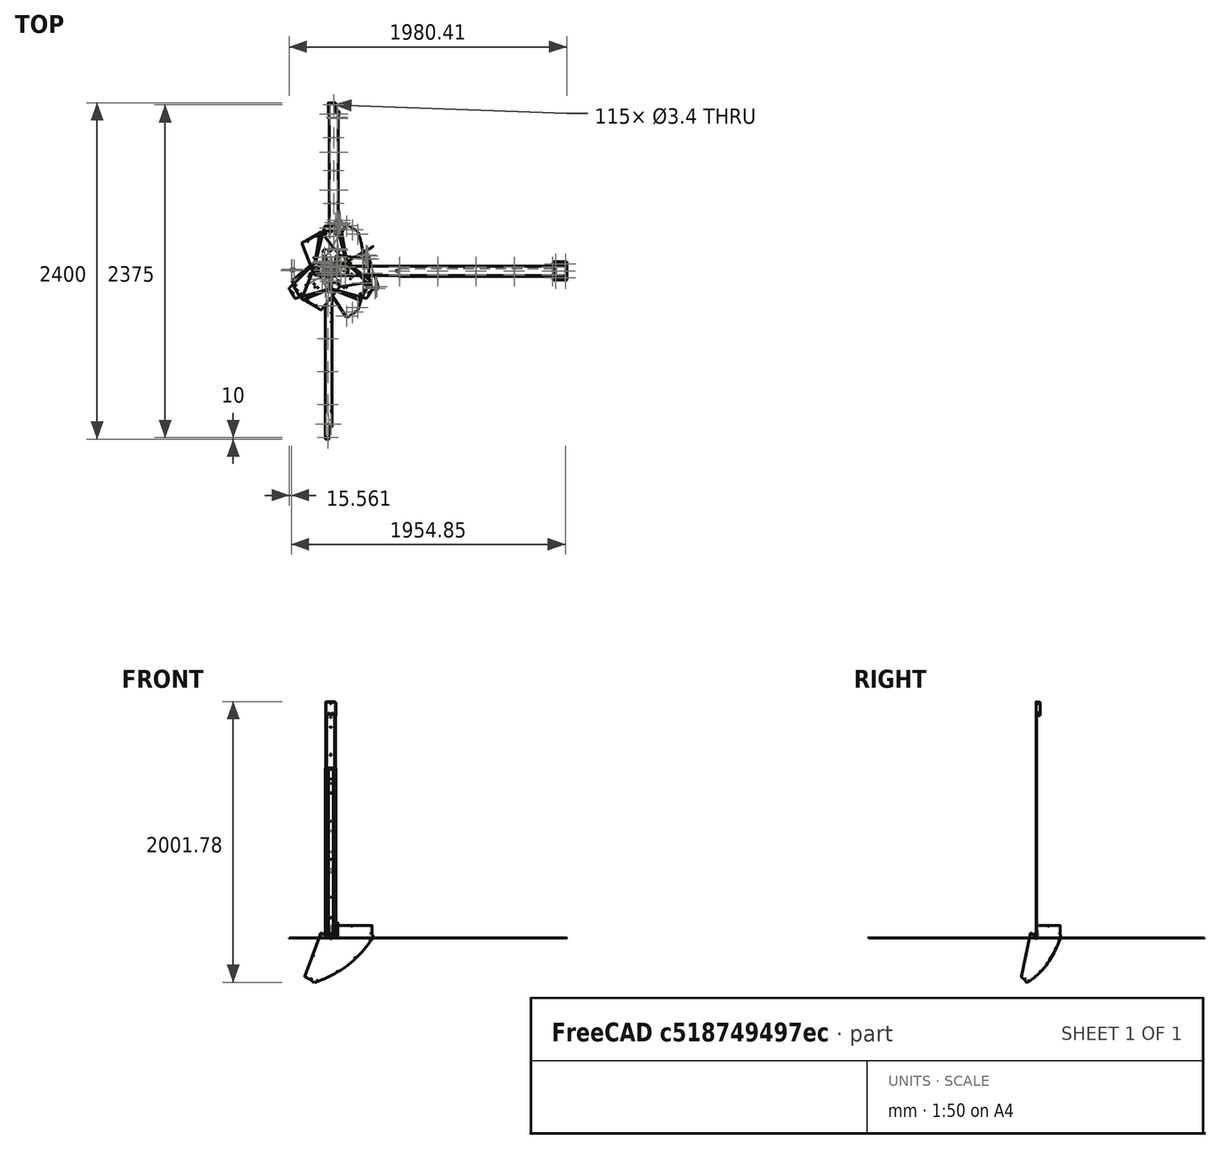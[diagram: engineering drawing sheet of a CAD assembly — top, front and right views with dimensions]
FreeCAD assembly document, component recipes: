
FREECAD ASSEMBLY — COMPONENT RECIPES ("composit_full_size3_ss_unfold")

This assembly document has 28 components, labeled P0..P27 below (a component is one placed body or linked part). 3 of them carry a construction recipe — the FreeCAD feature program that regenerates the part from scratch, quoted from this document or its linked companion documents; the rest are supplied as boundary geometry only. No exploded tour is included for this assembly.
COMPONENT P0 — recipe-attached ("Body", modeled in this document).
Construction recipe (the document's own serialized feature program — sketch geometry with constraints, then the solid features built on it; lengths are millimeters unless a unit is written):

FEATURE [PartDesign::FeatureBase] BaseFeature
  BaseFeature = -> Unfold
  Placement = pos=(0,0,0) rot=(-0.056475,0.056475,-0.996805;1.574rad)
  Suppressed = false
  expr: Placement = .BaseFeature.Placement
FEATURE [PartDesign::SubShapeBinder] Binder
  BindCopyOnChange = 0
  BindMode = 0
  ClaimChildren = false
  Context = -> Body [Binder.]
  Fuse = false
  MakeFace = true
  OffsetFill = false
  OffsetIntersection = false
  OffsetJoinType = 0
  OffsetOpenResult = false
  PartialLoad = false
  Relative = true
  Support = -> [Unfold_Sketch_bends]
  _Version = 2
FEATURE [Sketcher::SketchObject] Sketch
  AttachmentSupport = -> [XY_Plane]
  ExternalGeometry = -> [Binder]
  FullyConstrained = false
  MapMode = 5
  sketch-geometry (9):
    g0: Circle CenterX=172.913 CenterY=-294.074 CenterZ=0 NormalX=0 NormalY=0 NormalZ=1 AngleXU=0 Radius=1
    g1: Circle CenterX=4.76114 CenterY=-4.69033 CenterZ=0 NormalX=0 NormalY=0 NormalZ=1 AngleXU=0 Radius=1
    g2: Circle CenterX=4.76114 CenterY=4.69033 CenterZ=0 NormalX=0 NormalY=0 NormalZ=1 AngleXU=0 Radius=1
    g3: Circle CenterX=172.913 CenterY=294.074 CenterZ=0 NormalX=0 NormalY=0 NormalZ=1 AngleXU=0 Radius=1
    g4: LineSegment StartX=172.225 StartY=-294.474 StartZ=0 EndX=172.913 EndY=-294.074 EndZ=0
    g5: LineSegment StartX=4.07262 StartY=-5.0904 StartZ=0 EndX=4.76114 EndY=-4.69033 EndZ=0
    g6: LineSegment StartX=4.07262 StartY=5.0904 StartZ=0 EndX=4.76114 EndY=4.69033 EndZ=0
    g7: ArcOfCircle CenterX=1.01937 CenterY=5.2064e-12 CenterZ=0 NormalX=0 NormalY=0 NormalZ=1 AngleXU=0 Radius=6 StartAngle=5.25252 EndAngle=7.31385
    g8: LineSegment StartX=172.225 StartY=294.474 StartZ=0 EndX=172.913 EndY=294.074 EndZ=0
  constraints (25):
    c: Diameter(g0) = 2
    c: Equal(g0,g1)
    c: Equal(g1,g2)
    c: Equal(g2,g3)
    c: Coincident(g4,g-3)
    c: Coincident(g4,g0)
    c: Perpendicular(g-3,g4)
    c: Distance(g4) = 0.796314
    c: PointOnObject(g5,g-3)
    c: Perpendicular(g-3,g5)
    c: PointOnObject(g6,g-4)
    c: Perpendicular(g-4,g6)
    c: Coincident(g7,g-3)
    c: Coincident(g7,g-4)
    c: Coincident(g2,g6)
    c: PointOnObject(g2,g7)
    c: Radius(g7) = 6
    c: Coincident(g5,g1)
    c: PointOnObject(g1,g7)
    c: Equal(g5,g6)
    c: Equal(g6,g4)
    c: Coincident(g8,g-4)
    c: Coincident(g8,g3)
    c: Perpendicular(g-4,g8)
    c: Equal(g8,g6)
FEATURE [PartDesign::Pocket] Pocket
  BaseFeature = -> BaseFeature
  Direction = (0,0,-1)
  Length = 5
  Length2 = 5
  Midplane = true
  Placement = pos=(0,0,0) rot=(-0.056475,0.056475,-0.996805;1.574rad)
  Profile = -> Sketch
  ReferenceAxis = -> Sketch [N_Axis]
  Suppressed = false
  Type = 1
FEATURE [PartDesign::Body] Body
  BaseFeature = -> Unfold
  Group = -> [BaseFeature,Binder,Sketch,Pocket]
  Origin = -> Origin
  Tip = -> Pocket
COMPONENT P1 — recipe-attached ("pillar_top_Body", modeled in this document).
Construction recipe (the document's own serialized feature program — sketch geometry with constraints, then the solid features built on it; lengths are millimeters unless a unit is written):

FEATURE [PartDesign::SubShapeBinder] Binder001
  BindCopyOnChange = 0
  BindMode = 0
  ClaimChildren = false
  Context = -> Body001 [Binder001.]
  Fuse = false
  MakeFace = true
  OffsetFill = false
  OffsetIntersection = false
  OffsetJoinType = 0
  OffsetOpenResult = false
  PartialLoad = false
  Relative = true
  Support = -> [Unfold_Sketch_bends023]
  _Version = 2
  expr: Support = <<pillar_top_Sketch_bends>>._self
FEATURE [Sketcher::SketchObject] Sketch001
  AttachmentSupport = -> [XY_Plane001]
  ExternalGeometry = -> [Binder001]
  FullyConstrained = true
  MapMode = 5
  sketch-geometry (6):
    g0: Circle CenterX=-34.042 CenterY=-80.0841 CenterZ=0 NormalX=0 NormalY=0 NormalZ=1 AngleXU=0 Radius=1
    g1: Circle CenterX=34.042 CenterY=-80.0841 CenterZ=0 NormalX=0 NormalY=0 NormalZ=1 AngleXU=0 Radius=1
    g2: Circle CenterX=34.042 CenterY=-0.0840704 CenterZ=0 NormalX=0 NormalY=0 NormalZ=1 AngleXU=0 Radius=1
    g3: Circle CenterX=32 CenterY=1.95796 CenterZ=0 NormalX=0 NormalY=0 NormalZ=1 AngleXU=0 Radius=1
    g4: Circle CenterX=-32 CenterY=1.95796 CenterZ=0 NormalX=0 NormalY=0 NormalZ=1 AngleXU=0 Radius=1
    g5: Circle CenterX=-34.042 CenterY=-0.0840704 CenterZ=0 NormalX=0 NormalY=0 NormalZ=1 AngleXU=0 Radius=1
  constraints (12):
    c: Coincident(g0,g-5)
    c: Coincident(g1,g-6)
    c: Coincident(g2,g-6)
    c: Coincident(g3,g-3)
    c: Coincident(g4,g-4)
    c: Coincident(g5,g-5)
    c: Equal(g0,g1)
    c: Equal(g0,g2)
    c: Equal(g0,g3)
    c: Equal(g0,g5)
    c: Equal(g0,g4)
    c: Diameter(g0) = 2
FEATURE [PartDesign::FeatureBase] BaseFeature001
  BaseFeature = -> Unfold023
  Suppressed = false
  expr: BaseFeature = <<pillar_top_Unfold>>._self
FEATURE [PartDesign::Pocket] Pocket001
  BaseFeature = -> BaseFeature001
  Direction = (0,0,-1)
  Length = 5
  Length2 = 5
  Profile = -> Sketch001
  ReferenceAxis = -> Sketch001 [N_Axis]
  Reversed = true
  Suppressed = false
  Type = 0
FEATURE [PartDesign::Body] Body001  label="pillar_top_Body"
  Group = -> [BaseFeature001,Binder001,Sketch001,Pocket001]
  Origin = -> Origin001
  Tip = -> Pocket001
COMPONENT P2 — geometry summary ("Body002"; no construction recipe available for this part):
  bounding box: 102.9 x 96.0 x 0.5 mm
  tessellated surface: 412 triangles
  volume: 4717 mm^3 (96% of its bounding box)
  symmetry: mirror-symmetric across its z mid-plane
COMPONENT P3 — geometry summary ("pillar_Body"; no construction recipe available for this part):
  bounding box: 1684.0 x 75.0 x 2.0 mm
  tessellated surface: 1,560 triangles
  volume: 225558 mm^3 (89% of its bounding box)
  symmetry: 2-fold rotationally symmetric about the x axis; 2-fold rotationally symmetric about the y axis; 2-fold rotationally symmetric about the z axis; mirror-symmetric across its x mid-plane, y mid-plane, z mid-plane
COMPONENT P4 — geometry summary ("pillar_bottom_Body"; no construction recipe available for this part):
  bounding box: 131.1 x 101.0 x 2.0 mm
  tessellated surface: 800 triangles
  volume: 11774 mm^3 (44% of its bounding box)
  symmetry: mirror-symmetric across its z mid-plane
COMPONENT P5 — geometry summary ("dec_corner_Body"; no construction recipe available for this part):
  bounding box: 1113.0 x 56.5 x 0.5 mm
  tessellated surface: 572 triangles
  volume: 31373 mm^3 (100% of its bounding box)
  symmetry: 2-fold rotationally symmetric about the x axis; 2-fold rotationally symmetric about the y axis; 2-fold rotationally symmetric about the z axis; mirror-symmetric across its x mid-plane, y mid-plane, z mid-plane
COMPONENT P6 — geometry summary ("basement_amplifier_old_body"; no construction recipe available for this part):
  bounding box: 245.0 x 58.2 x 2.0 mm
  tessellated surface: 736 triangles
  volume: 27799 mm^3 (98% of its bounding box)
  symmetry: 2-fold rotationally symmetric about the x axis; 2-fold rotationally symmetric about the y axis; mirror-symmetric across its y mid-plane, z mid-plane
COMPONENT P7 — geometry summary ("door_conn_body"; no construction recipe available for this part):
  bounding box: 1200.0 x 78.8 x 1.0 mm
  tessellated surface: 1,212 triangles
  volume: 75758 mm^3 (80% of its bounding box)
  symmetry: mirror-symmetric across its z mid-plane
COMPONENT P8 — geometry summary ("door_base_pillar_to_hor_fix_body"; no construction recipe available for this part):
  bounding box: 44.9 x 40.5 x 1.0 mm
  tessellated surface: 472 triangles
  volume: 1128 mm^3 (62% of its bounding box)
  symmetry: mirror-symmetric across its z mid-plane
COMPONENT P9 — geometry summary ("door_hor_body"; no construction recipe available for this part):
  bounding box: 256.0 x 97.5 x 1.0 mm
  tessellated surface: 528 triangles
  volume: 9271 mm^3 (37% of its bounding box)
  symmetry: mirror-symmetric across its z mid-plane
COMPONENT P10 — geometry summary ("sink_material_0.30ansi"; no construction recipe available for this part):
  bounding box: 589.7 x 237.9 x 89.4 mm
  tessellated surface: 1,040 triangles
  volume: 66854 mm^3 (1% of its bounding box)
  symmetry: mirror-symmetric across its x mid-plane
COMPONENT P11 — geometry summary ("top_dec_corner_0.30ansi"; no construction recipe available for this part):
  bounding box: 96.0 x 75.5 x 29.0 mm
  tessellated surface: 448 triangles
  volume: 4725 mm^3 (2% of its bounding box)
COMPONENT P12 — geometry summary ("pillar_bottom_material_0.30ansi"; no construction recipe available for this part):
  bounding box: 101.0 x 80.0 x 25.0 mm
  tessellated surface: 792 triangles
  volume: 11019 mm^3 (5% of its bounding box)
COMPONENT P13 — geometry summary ("pillar_material_0.30ansi"; no construction recipe available for this part):
  bounding box: 1684.0 x 75.0 x 19.0 mm
  tessellated surface: 1,560 triangles
  volume: 229601 mm^3 (10% of its bounding box)
  symmetry: mirror-symmetric across its x mid-plane
COMPONENT P14 — recipe-attached ("dec_corner_0.30ansi", modeled in this document).
Construction recipe (the document's own serialized feature program — sketch geometry with constraints, then the solid features built on it; lengths are millimeters unless a unit is written):

FEATURE [Part::Feature] Unfold017
  Placement = pos=(0,0,0) rot=(0,0,1;0.523599rad)
  shape: bbox 481.5 x 552.9 x 2 mm, 69 faces (baked)
FEATURE [PartDesign::FeatureAdditivePython] PDW_Add001  # link proxy (typed FeaturePython)
  Body = Body013
  ClaimChildren = true
  EditPlacementAdjustments = false
  Enabled = 1
  LinkedObject = -> Unfold017
  MeshTolerance = 0.1
  PatternBaseOffset = 0
  PatternBaseScale = 1
  PatternBaseScaleXYZ = (1,1,1)
  PatternOffsetCut = false
  PatternOffsetIntersection = false
  PatternOffsetJoin = 0
  PatternOffsetMode = 0
  PatternOffsetSelfIntersection = false
  PatternOperation = 0
  PatternOperationDefault = None
  PatternScaleCut = false
  PatternShapeOffset = 0
  PatternShapeScale = 1
  PatternShapeScaleXYZ = (1,1,1)
  PatternToolOffset = 0
  PatternToolScale = 1
  PatternToolScaleXYZ = (1,1,1)
  RefineMesh = true
  ShapeManagement = 0
  ShowMeshProps = false
  ShowOffsetProps = false
  ShowScaleProps = false
  ShowWarnings = true
  Suppressed = false
  TipBaseOffset = 0
  TipBaseScale = 1
  TipBaseScaleXYZ = (1,1,1)
  TipOffsetCut = false
  TipOffsetIntersection = false
  TipOffsetJoin = 0
  TipOffsetMode = 0
  TipOffsetSelfIntersection = false
  TipOperation = 0
  TipOperationDefault = Fuse
  TipScaleCut = false
  TipShapeOffset = 0
  TipShapeScale = 1
  TipShapeScaleXYZ = (1,1,1)
  TipTool = -> Unfold017
  TipToolOffset = 0
  TipToolScale = 1
  TipToolScaleXYZ = (1,1,1)
  Type = Additive
  UsePatternBaseAddSubShape = false
  UsePatternToolAddSubShape = false
  UseTipBaseAddSubShape = false
  UseTipToolAddSubShape = false
  Version = 0.2023.08.13
FEATURE [Sketcher::SketchObject] Unfold_Sketch_bends017  label="basement2_amplifier_bends"
  FullyConstrained = false
  sketch-geometry (6):
    g0: LineSegment StartX=48.4571 StartY=82.0288 StartZ=0 EndX=273.448 EndY=46.699 EndZ=0
    g1: LineSegment StartX=273.448 StartY=-46.699 StartZ=0 EndX=48.4571 EndY=-82.0288 EndZ=0
    g2: LineSegment StartX=-96.2817 StartY=260.163 StartZ=0 EndX=46.8104 EndY=82.9795 EndZ=0
    g3: LineSegment StartX=46.8104 StartY=-82.9795 StartZ=0 EndX=-96.2817 EndY=-260.163 EndZ=0
    g4: LineSegment StartX=-95.2675 StartY=0.950723 StartZ=0 EndX=-177.167 EndY=213.464 EndZ=0
    g5: LineSegment StartX=-177.167 StartY=-213.464 StartZ=0 EndX=-95.2675 EndY=-0.950723 EndZ=0
FEATURE [Sketcher::SketchObject] Unfold_Sketch017  label="basement2_amplifier_Sketch"
  ExternalGeometry = -> [Unfold_Sketch_bends017]
  FullyConstrained = false
  sketch-geometry (79):
    g0: ArcOfCircle CenterX=70.1267 CenterY=101.256 CenterZ=0 NormalX=0 NormalY=0 NormalZ=1 AngleXU=2.98584 Radius=10 StartAngle=4.71239 EndAngle=5.91534
    g1: LineSegment StartX=268.589 StartY=80.2148 StartZ=0 EndX=71.678 EndY=111.135 EndZ=0
    g2: ArcOfCircle CenterX=267.037 CenterY=70.3358 CenterZ=0 NormalX=0 NormalY=0 NormalZ=1 AngleXU=2.98584 Radius=10 StartAngle=3.14159 EndAngle=4.71239
    g3: LineSegment StartX=61.4665 StartY=106.256 StartZ=0 EndX=48.8226 EndY=84.3564 EndZ=0
    g4: LineSegment StartX=48.0916 StartY=79.7011 StartZ=0 EndX=48.8226 EndY=84.3564 EndZ=0
    g5: LineSegment StartX=48.0916 StartY=79.7011 StartZ=0 EndX=46.188 EndY=80 EndZ=0
    g6: LineSegment StartX=46.188 StartY=80 StartZ=0 EndX=44.9774 EndY=81.4991 EndZ=0
    g7: LineSegment StartX=48.6435 StartY=84.4599 StartZ=0 EndX=61.2873 EndY=106.36 EndZ=0
    g8: ArcOfCircle CenterX=52.6271 CenterY=111.36 CenterZ=0 NormalX=0 NormalY=0 NormalZ=1 AngleXU=-0.891442 Radius=10 StartAngle=0.367843 EndAngle=1.5708
    g9: ArcOfCircle CenterX=-72.6061 CenterY=266.429 CenterZ=0 NormalX=0 NormalY=0 NormalZ=1 AngleXU=-0.891442 Radius=10 StartAngle=1.5708 EndAngle=3.14159
    g10: LineSegment StartX=60.4069 StartY=117.643 StartZ=0 EndX=-64.8263 EndY=272.712 EndZ=0
    g11: LineSegment StartX=48.6435 StartY=84.4599 StartZ=0 EndX=44.9774 EndY=81.4991 EndZ=0
    g12: LineSegment StartX=-98.1147 StartY=258.682 StartZ=0 EndX=-78.889 EndY=274.209 EndZ=0
    g13: LineSegment StartX=-98.1147 StartY=258.682 StartZ=0 EndX=-174.968 EndY=214.311 EndZ=0
    g14: LineSegment StartX=-198.027 StartY=205.424 StartZ=0 EndX=-174.968 EndY=214.311 EndZ=0
    g15: ArcOfCircle CenterX=-194.431 CenterY=196.093 CenterZ=0 NormalX=0 NormalY=0 NormalZ=1 AngleXU=-1.20295 Radius=10 StartAngle=3.14159 EndAngle=4.71239
    g16: LineSegment StartX=-203.762 StartY=192.497 StartZ=0 EndX=-132.085 EndY=6.50739 EndZ=0
    g17: ArcOfCircle CenterX=-122.754 CenterY=10.1034 CenterZ=0 NormalX=0 NormalY=0 NormalZ=1 AngleXU=-1.20295 Radius=10 StartAngle=4.71239 EndAngle=5.91534
    g18: LineSegment StartX=-122.754 StartY=0.103426 StartZ=0 EndX=-97.4661 EndY=0.103426 EndZ=0
    g19: LineSegment StartX=-93.069 StartY=1.79802 StartZ=0 EndX=-97.4661 EndY=0.103426 EndZ=0
    g20: LineSegment StartX=-93.069 StartY=1.79802 StartZ=0 EndX=-92.376 EndY=-7.26482e-10 EndZ=0
    g21: LineSegment StartX=-92.376 StartY=-7.26482e-10 StartZ=0 EndX=-93.069 EndY=-1.79802 EndZ=0
    g22: LineSegment StartX=-97.4661 StartY=-0.103426 StartZ=0 EndX=-93.069 EndY=-1.79802 EndZ=0
    g23: LineSegment StartX=-97.4661 StartY=-0.103426 StartZ=0 EndX=-122.754 EndY=-0.103426 EndZ=0
    g24: ArcOfCircle CenterX=-122.754 CenterY=-10.1034 CenterZ=0 NormalX=0 NormalY=0 NormalZ=1 AngleXU=1.20295 Radius=10 StartAngle=0.367843 EndAngle=1.5708
    g25: LineSegment StartX=-132.085 StartY=-6.50739 StartZ=0 EndX=-203.762 EndY=-192.497 EndZ=0
    g26: ArcOfCircle CenterX=-194.431 CenterY=-196.093 CenterZ=0 NormalX=0 NormalY=0 NormalZ=1 AngleXU=1.20295 Radius=10 StartAngle=1.5708 EndAngle=3.14159
    g27: LineSegment StartX=-174.968 StartY=-214.311 StartZ=0 EndX=-198.027 EndY=-205.424 EndZ=0
    g28: LineSegment StartX=-174.968 StartY=-214.311 StartZ=0 EndX=-98.1147 EndY=-258.682 EndZ=0
    g29: LineSegment StartX=-78.889 StartY=-274.209 StartZ=0 EndX=-98.1147 EndY=-258.682 EndZ=0
    g30: ArcOfCircle CenterX=-72.6061 CenterY=-266.429 CenterZ=0 NormalX=0 NormalY=0 NormalZ=1 AngleXU=0.891442 Radius=10 StartAngle=3.14159 EndAngle=4.71239
    g31: LineSegment StartX=-64.8263 StartY=-272.712 StartZ=0 EndX=60.4069 EndY=-117.643 EndZ=0
    g32: ArcOfCircle CenterX=52.6271 CenterY=-111.36 CenterZ=0 NormalX=0 NormalY=0 NormalZ=1 AngleXU=0.891442 Radius=10 StartAngle=4.71239 EndAngle=5.91534
    g33: LineSegment StartX=61.2873 StartY=-106.36 StartZ=0 EndX=48.6435 EndY=-84.4599 EndZ=0
    g34: LineSegment StartX=44.9774 StartY=-81.4991 StartZ=0 EndX=48.6435 EndY=-84.4599 EndZ=0
    g35: LineSegment StartX=44.9774 StartY=-81.4991 StartZ=0 EndX=46.188 EndY=-80 EndZ=0
    g36: LineSegment StartX=46.188 StartY=-80 StartZ=0 EndX=48.0916 EndY=-79.7011 EndZ=0
    g37: LineSegment StartX=48.8226 StartY=-84.3564 StartZ=0 EndX=48.0916 EndY=-79.7011 EndZ=0
    g38: LineSegment StartX=48.8226 StartY=-84.3564 StartZ=0 EndX=61.4665 EndY=-106.256 EndZ=0
    g39: ArcOfCircle CenterX=70.1267 CenterY=-101.256 CenterZ=0 NormalX=0 NormalY=0 NormalZ=1 AngleXU=-2.98584 Radius=10 StartAngle=0.367843 EndAngle=1.5708
    g40: LineSegment StartX=71.678 StartY=-111.135 StartZ=0 EndX=268.589 EndY=-80.2148 EndZ=0
    g41: ArcOfCircle CenterX=267.037 CenterY=-70.3358 CenterZ=0 NormalX=0 NormalY=0 NormalZ=1 AngleXU=-2.98584 Radius=10 StartAngle=1.5708 EndAngle=3.14159
    g42: LineSegment StartX=273.083 StartY=-44.3713 StartZ=0 EndX=276.916 EndY=-68.7846 EndZ=0
    g43: LineSegment StartX=273.083 StartY=44.3713 StartZ=0 EndX=273.083 EndY=-44.3713 EndZ=0
    g44: LineSegment StartX=276.916 StartY=68.7846 StartZ=0 EndX=273.083 EndY=44.3713 EndZ=0
    g45: Circle CenterX=34.575 CenterY=34.575 CenterZ=0 NormalX=0 NormalY=0 NormalZ=1 AngleXU=-1.5708 Radius=5.4
    g46: Circle CenterX=-34.575 CenterY=-34.575 CenterZ=0 NormalX=0 NormalY=0 NormalZ=1 AngleXU=-1.5708 Radius=5.4
    g47: Circle CenterX=34.575 CenterY=-34.575 CenterZ=0 NormalX=0 NormalY=0 NormalZ=1 AngleXU=-1.5708 Radius=5.4
    g48: Circle CenterX=-34.575 CenterY=34.575 CenterZ=0 NormalX=0 NormalY=0 NormalZ=1 AngleXU=-1.5708 Radius=5.4
    g49: Circle CenterX=265 CenterY=-36 CenterZ=0 NormalX=0 NormalY=0 NormalZ=1 AngleXU=-1.5708 Radius=2.5
    g50: Circle CenterX=265 CenterY=36 CenterZ=0 NormalX=0 NormalY=0 NormalZ=1 AngleXU=1.5708 Radius=2.5
    g51: Circle CenterX=55.7258 CenterY=68.9742 CenterZ=0 NormalX=0 NormalY=0 NormalZ=1 AngleXU=1.5708 Radius=2.5
    g52: Circle CenterX=140.207 CenterY=56.173 CenterZ=0 NormalX=0 NormalY=0 NormalZ=1 AngleXU=1.5708 Radius=2.5
    g53: Circle CenterX=-21.4561 CenterY=149.509 CenterZ=0 NormalX=0 NormalY=0 NormalZ=1 AngleXU=0.523599 Radius=2.5
    g54: Circle CenterX=-101.323 CenterY=247.497 CenterZ=0 NormalX=0 NormalY=0 NormalZ=1 AngleXU=0.523599 Radius=2.5
    g55: Circle CenterX=-87.5963 CenterY=13.7728 CenterZ=0 NormalX=0 NormalY=0 NormalZ=1 AngleXU=-2.61799 Radius=2.5
    g56: Circle CenterX=140.207 CenterY=-56.173 CenterZ=0 NormalX=0 NormalY=0 NormalZ=1 AngleXU=-1.5708 Radius=2.5
    g57: Circle CenterX=55.7258 CenterY=-68.9742 CenterZ=0 NormalX=0 NormalY=0 NormalZ=1 AngleXU=-1.5708 Radius=2.5
    g58: Circle CenterX=-87.5963 CenterY=-13.7728 CenterZ=0 NormalX=0 NormalY=0 NormalZ=1 AngleXU=2.61799 Radius=2.5
    g59: Circle CenterX=-21.4561 CenterY=-149.509 CenterZ=0 NormalX=0 NormalY=0 NormalZ=1 AngleXU=-0.523599 Radius=2.5
    g60: Circle CenterX=31.8705 CenterY=-82.747 CenterZ=0 NormalX=0 NormalY=0 NormalZ=1 AngleXU=-0.523599 Radius=2.5
    g61: Circle CenterX=31.8705 CenterY=82.747 CenterZ=0 NormalX=0 NormalY=0 NormalZ=1 AngleXU=0.523599 Radius=2.5
    g62: Circle CenterX=-118.751 CenterY=93.336 CenterZ=0 NormalX=0 NormalY=0 NormalZ=1 AngleXU=-2.61799 Radius=2.5
    g63: Circle CenterX=-163.677 CenterY=211.497 CenterZ=0 NormalX=0 NormalY=0 NormalZ=1 AngleXU=-2.61799 Radius=2.5
    g64: Circle CenterX=-118.751 CenterY=-93.336 CenterZ=0 NormalX=0 NormalY=0 NormalZ=1 AngleXU=2.61799 Radius=2.5
    g65: Circle CenterX=-101.323 CenterY=-247.497 CenterZ=0 NormalX=0 NormalY=0 NormalZ=1 AngleXU=-0.523599 Radius=2.5
    g66: Circle CenterX=-163.677 CenterY=-211.497 CenterZ=0 NormalX=0 NormalY=0 NormalZ=1 AngleXU=2.61799 Radius=2.5
    g67: LineSegment StartX=48.4571 StartY=-82.0288 StartZ=0 EndX=50.4329 EndY=-81.7185 EndZ=0
    g68: LineSegment StartX=48.4571 StartY=82.0288 StartZ=0 EndX=50.4329 EndY=81.7185 EndZ=0
    g69: LineSegment StartX=273.448 StartY=46.699 StartZ=0 EndX=271.473 EndY=47.0092 EndZ=0
    g70: LineSegment StartX=273.448 StartY=-46.699 StartZ=0 EndX=271.473 EndY=-47.0092 EndZ=0
    g71: LineSegment StartX=-176.447 StartY=211.597 StartZ=0 EndX=-177.167 EndY=213.464 EndZ=0
    g72: LineSegment StartX=45.5538 StartY=84.5354 StartZ=0 EndX=46.8104 EndY=82.9795 EndZ=0
    g73: LineSegment StartX=-95.0251 StartY=258.607 StartZ=0 EndX=-96.2817 EndY=260.163 EndZ=0
    g74: LineSegment StartX=-95.2675 StartY=0.950723 StartZ=0 EndX=-95.9868 EndY=2.81693 EndZ=0
    g75: LineSegment StartX=-177.167 StartY=-213.464 StartZ=0 EndX=-176.447 EndY=-211.597 EndZ=0
    g76: LineSegment StartX=-95.9868 StartY=-2.81693 StartZ=0 EndX=-95.2675 EndY=-0.950723 EndZ=0
    g77: LineSegment StartX=46.8104 StartY=-82.9795 StartZ=0 EndX=45.5538 EndY=-84.5354 EndZ=0
    g78: LineSegment StartX=-95.0251 StartY=-258.607 StartZ=0 EndX=-96.2817 EndY=-260.163 EndZ=0
  constraints (81):
    c: Coincident(g67,g-5)
    c: PointOnObject(g67,g-5)
    c: Coincident(g68,g-7)
    c: PointOnObject(g68,g-7)
    c: Coincident(g69,g-7)
    c: PointOnObject(g69,g-7)
    c: Coincident(g70,g-5)
    c: PointOnObject(g70,g-5)
    c: Equal(g67,g68)
    c: Equal(g68,g69)
    c: Equal(g69,g70)
    c: Distance(g67) = 2
    c: Equal(g74,g71)
    c: Equal(g71,g72)
    c: Equal(g72,g73)
    c: Equal(g67,g74) = 2
    c: Coincident(g74,g-4)
    c: PointOnObject(g74,g-4)
    c: Coincident(g71,g-4)
    c: PointOnObject(g71,g-4)
    c: Coincident(g72,g-8)
    c: PointOnObject(g72,g-8)
    c: Coincident(g73,g-8)
    c: PointOnObject(g73,g-8)
    c: Equal(g75,g76)
    c: Equal(g76,g77)
    c: Equal(g77,g78)
    c: Equal(g67,g75) = 2
    c: Coincident(g78,g-6)
    c: PointOnObject(g78,g-6)
    c: Coincident(g75,g-3)
    c: PointOnObject(g75,g-3)
    c: Coincident(g76,g-3)
    c: PointOnObject(g76,g-3)
    c: Coincident(g77,g-6)
    c: PointOnObject(g77,g-6)
    c: Coincident(g25,g26)
    c: Coincident(g15,g16)
    c: Coincident(g26,g27)
    c: Coincident(g14,g15)
    c: Coincident(g27,g28)
    c: Coincident(g13,g14)
    c: Coincident(g24,g25)
    c: Coincident(g16,g17)
    c: Coincident(g23,g24)
    c: Coincident(g17,g18)
    c: Coincident(g28,g29)
    c: Coincident(g12,g13)
    c: Coincident(g22,g23)
    c: Coincident(g18,g19)
    c: Coincident(g21,g22)
    c: Coincident(g19,g20)
    c: Coincident(g20,g21)
    c: Coincident(g29,g30)
    c: Coincident(g9,g12)
    c: Coincident(g30,g31)
    c: Coincident(g9,g10)
    c: Coincident(g34,g35)
    c: Coincident(g6,g11)
    c: Coincident(g35,g36)
    c: Coincident(g5,g6)
    c: Coincident(g36,g37)
    c: Coincident(g4,g5)
    c: Coincident(g33,g34)
    c: Coincident(g7,g11)
    c: Coincident(g37,g38)
    c: Coincident(g3,g4)
    c: Coincident(g31,g32)
    c: Coincident(g8,g10)
    c: Coincident(g32,g33)
    c: Coincident(g7,g8)
    c: Coincident(g38,g39)
    c: Coincident(g0,g3)
    c: Coincident(g39,g40)
    c: Coincident(g0,g1)
    c: Coincident(g40,g41)
    c: Coincident(g1,g2)
    c: Coincident(g42,g43)
    c: Coincident(g43,g44)
    c: Coincident(g41,g42)
    c: Coincident(g2,g44)
FEATURE [PartDesign::Body] Body013  label="basement_amplifier_bottom_body"
  Group = -> [PDW_Add001,Unfold017,Unfold_Sketch017,Unfold_Sketch_bends017]
  Origin = -> Origin013
  Tip = -> PDW_Add001
COMPONENT P15 — geometry summary ("pillar_top_element_0.30ansi"; no construction recipe available for this part):
  bounding box: 84.0 x 72.0 x 70.0 mm
  tessellated surface: 966 triangles
  volume: 26396 mm^3 (6% of its bounding box)
COMPONENT P16 — geometry summary ("basement_amplifier_old"; no construction recipe available for this part):
  bounding box: 245.0 x 36.0 x 15.0 mm
  tessellated surface: 824 triangles
  volume: 28415 mm^3 (21% of its bounding box)
  symmetry: mirror-symmetric across its x mid-plane, y mid-plane
COMPONENT P17 — geometry summary ("door_base_pillar_material_0.45ansi"; no construction recipe available for this part):
  bounding box: 1200.0 x 29.9 x 19.7 mm
  tessellated surface: 704 triangles
  volume: 47242 mm^3 (7% of its bounding box)
COMPONENT P18 — geometry summary ("basement_amplifier_material_0.30ansi001"; no construction recipe available for this part):
  bounding box: 584.8 x 506.5 x 29.3 mm
  tessellated surface: 3,000 triangles
  volume: 267234 mm^3 (3% of its bounding box)
  symmetry: mirror-symmetric across its x mid-plane
COMPONENT P19 — geometry summary ("basement2_amplifier_material_0.30ansi"; no construction recipe available for this part):
  bounding box: 533.2 x 463.7 x 34.0 mm
  tessellated surface: 2,344 triangles
  volume: 289000 mm^3 (3% of its bounding box)
  symmetry: mirror-symmetric across its x mid-plane
COMPONENT P20 — geometry summary ("top_amplifier_cornrer_material_0.50ansi"; no construction recipe available for this part):
  bounding box: 43.4 x 42.2 x 34.0 mm
  tessellated surface: 548 triangles
  volume: 3298 mm^3 (5% of its bounding box)
COMPONENT P21 — geometry summary ("pillar2_material_0.50ansi"; no construction recipe available for this part):
  bounding box: 1686.0 x 58.0 x 14.0 mm
  tessellated surface: 1,160 triangles
  volume: 195131 mm^3 (14% of its bounding box)
  symmetry: mirror-symmetric across its x mid-plane
COMPONENT P22 — geometry summary ("pillar2_bottom_material_0.50ansi"; no construction recipe available for this part):
  bounding box: 110.0 x 101.0 x 25.0 mm
  tessellated surface: 844 triangles
  volume: 11895 mm^3 (4% of its bounding box)
COMPONENT P23 — geometry summary ("pillar3"; no construction recipe available for this part):
  bounding box: 1684.0 x 36.6 x 19.0 mm
  tessellated surface: 1,732 triangles
  volume: 228487 mm^3 (20% of its bounding box)
  symmetry: 2-fold rotationally symmetric about the y axis; mirror-symmetric across its x mid-plane, z mid-plane
COMPONENT P24 — geometry summary ("pillar3_hat_fix"; no construction recipe available for this part):
  bounding box: 84.0 x 70.0 x 28.6 mm
  tessellated surface: 536 triangles
  volume: 7336 mm^3 (4% of its bounding box)
COMPONENT P25 — geometry summary ("pilllar3_dec_corner_mirror"; no construction recipe available for this part):
  bounding box: 1214.0 x 37.1 x 21.0 mm
  tessellated surface: 1,044 triangles
  volume: 34281 mm^3 (4% of its bounding box)
  symmetry: mirror-symmetric across its z mid-plane
COMPONENT P26 — geometry summary ("pilllar3_dec_corner"; no construction recipe available for this part):
  bounding box: 1214.0 x 37.1 x 21.0 mm
  tessellated surface: 1,044 triangles
  volume: 34281 mm^3 (4% of its bounding box)
  symmetry: mirror-symmetric across its z mid-plane
COMPONENT P27 — geometry summary ("Unfold042"; no construction recipe available for this part):
  bounding box: 53.0 x 50.9 x 1.0 mm
  tessellated surface: 484 triangles
  volume: 2590 mm^3 (96% of its bounding box)
  symmetry: 2-fold rotationally symmetric about the x axis; 2-fold rotationally symmetric about the y axis; 2-fold rotationally symmetric about the z axis; mirror-symmetric across its y mid-plane, z mid-plane
PROVENANCE & LICENSES
A FreeCAD (.FCStd) document from a public repository crawl; recipes are the document's own serialized feature recipes (and, for linked parts, companion documents' recipes).
License: as declared in the source repository (recorded in the dataset sidecar).
